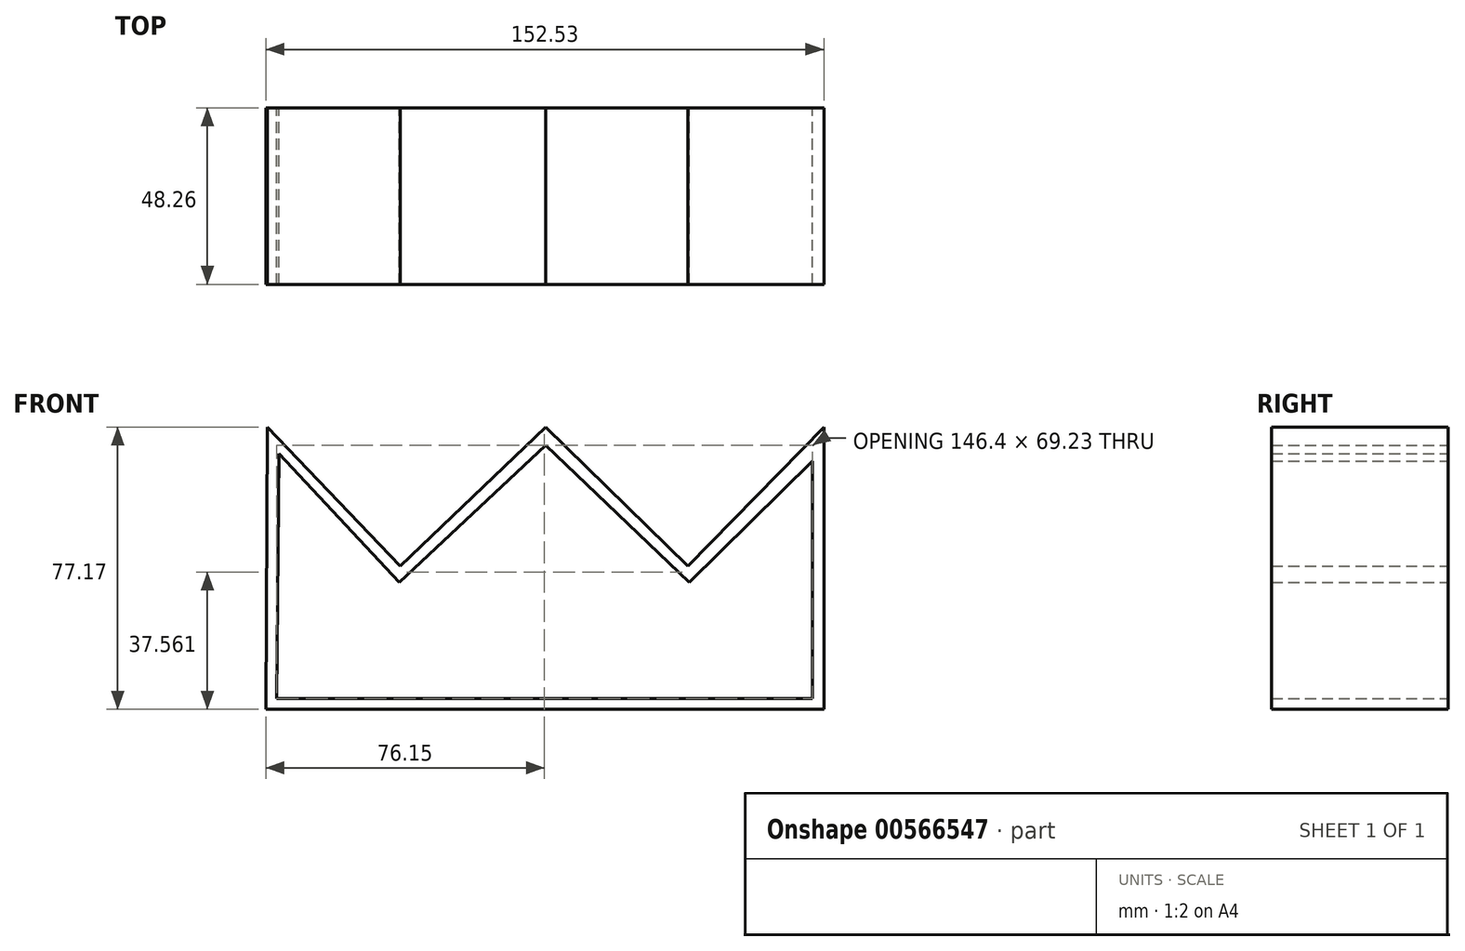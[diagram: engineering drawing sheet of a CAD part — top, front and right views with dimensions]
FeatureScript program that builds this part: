
annotation { "Feature Type Name" : "Feature", "Feature Type Description" : "" }
export const myFeature = defineFeature(function(context is Context, id is Id, definition is map)
    precondition{}
    {
        {
            var Q0;
            Q0=qCreatedBy(makeId("Front.planeOp"),FACE);
            var sketch = newSketch(context, id + "F0", { "sketchPlane" : qUnion([Q0])});
            skLineSegment(sketch, "E0", {"start": v(-76.5, -39.15) * mm, "end": v(76.04, -39.15) * mm});
            skLineSegment(sketch, "E1", {"start": v(76.04, -39.15) * mm, "end": v(76.04, 38.02) * mm});
            skLineSegment(sketch, "E2", {"start": v(38.81, 0) * mm, "end": v(76.04, 38.02) * mm});
            skLineSegment(sketch, "E3", {"start": v(0, 38.02) * mm, "end": v(38.81, 0) * mm});
            skLineSegment(sketch, "E4", {"start": v(0, 38.02) * mm, "end": v(-39.72, 0) * mm});
            skLineSegment(sketch, "E5", {"start": v(-39.72, 0) * mm, "end": v(-76.11, 38.02) * mm});
            skLineSegment(sketch, "E6", {"start": v(-76.11, 38.02) * mm, "end": v(-76.5, -39.15) * mm});
            skSolve(sketch);
        }
        {
            var Q0;
            Q0=qCreatedBy(makeId("Front.planeOp"),FACE);
            var sketch = newSketch(context, id + "F1", { "sketchPlane" : qUnion([Q0])});
            skLineSegment(sketch, "E7", {"start": v(-73.54, -36.2) * mm, "end": v(72.86, -36.2) * mm});
            skLineSegment(sketch, "E8", {"start": v(72.86, -36.2) * mm, "end": v(72.86, 28.71) * mm});
            skLineSegment(sketch, "E9", {"start": v(72.86, 28.71) * mm, "end": v(39.27, -4.43) * mm});
            skLineSegment(sketch, "E10", {"start": v(39.27, -4.43) * mm, "end": v(0, 33.03) * mm});
            skLineSegment(sketch, "E11", {"start": v(0, 33.03) * mm, "end": v(-39.95, -4.43) * mm});
            skLineSegment(sketch, "E12", {"start": v(-39.95, -4.43) * mm, "end": v(-72.86, 30.68) * mm});
            skLineSegment(sketch, "E13", {"start": v(-72.86, 30.68) * mm, "end": v(-73.54, -36.2) * mm});
            skSolve(sketch);
        }
        {
            var Q0;
            Q0=makeQuery(id+"F0.imprint","IMPRINT",FACE,{"disambiguationData":[TD([[makeQuery(id+"F0.imprint","IMPRINT",EDGE,{"derivedFrom":sQuery(id+"F0.wireOp",EDGE,"E0")}),1.0]])]});
            extrude(context, id + "F2", {"entities" : qUnion([Q0]), "depth" : 48.26 * mm, "offsetDistance" : 25.4 * mm});
        }
        {
            var Q0;
            Q0=makeQuery(id+"F1.imprint","IMPRINT",FACE,{"disambiguationData":[TD([[makeQuery(id+"F1.imprint","IMPRINT",EDGE,{"derivedFrom":sQuery(id+"F1.wireOp",EDGE,"E7")}),1.0]])]});
            extrude(context, id + "F3", {"entities" : qUnion([Q0]), "operationType" : NewBodyOperationType.REMOVE, "depth" : 108.97 * mm, "offsetDistance" : 25.4 * mm});
        }
    });
